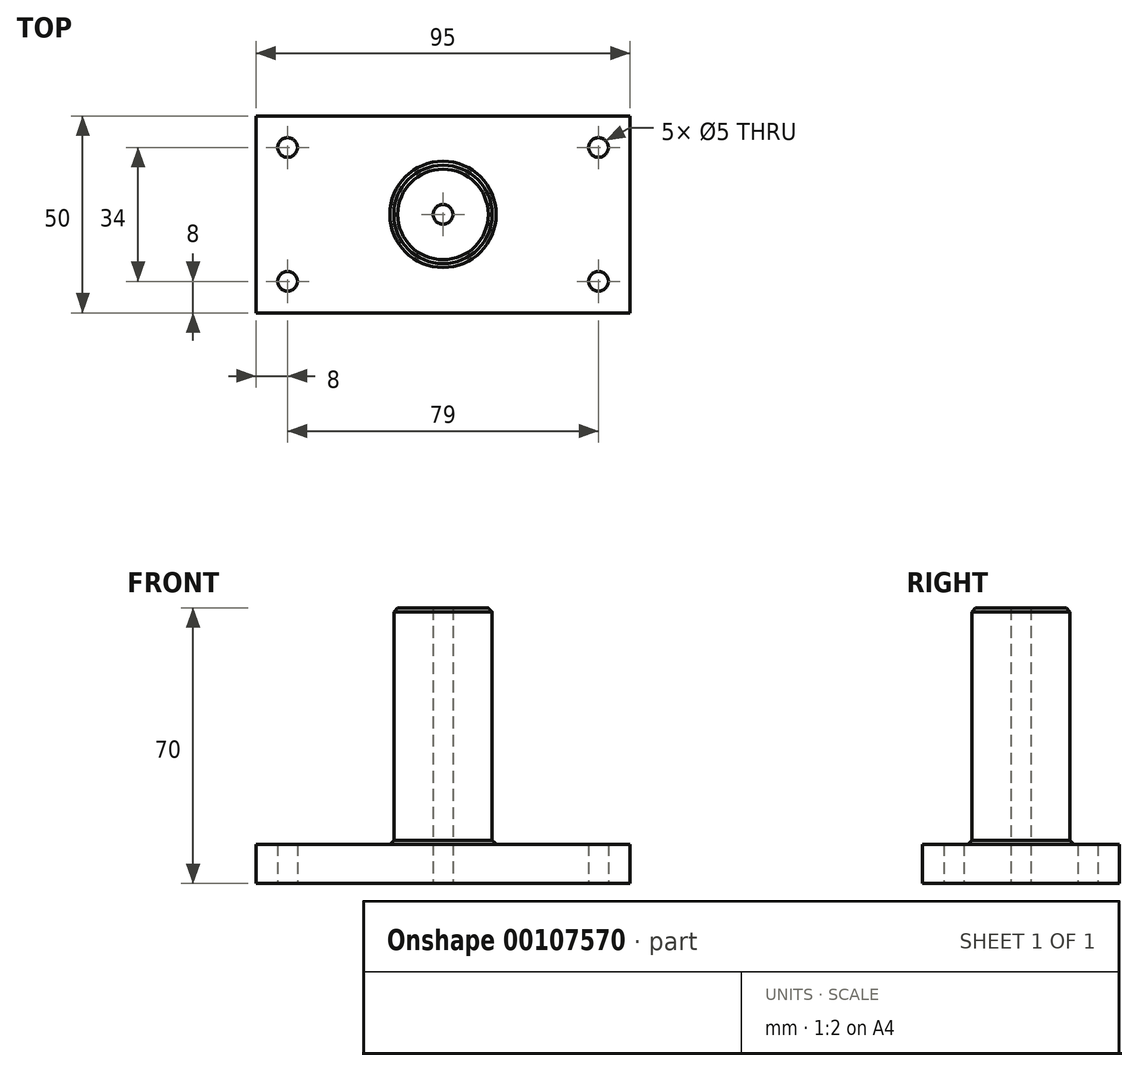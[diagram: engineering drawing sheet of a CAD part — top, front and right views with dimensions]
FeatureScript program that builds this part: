
annotation { "Feature Type Name" : "Feature", "Feature Type Description" : "" }
export const myFeature = defineFeature(function(context is Context, id is Id, definition is map)
    precondition{}
    {
        {
            var Q0;
            Q0=qCreatedBy(makeId("Top.planeOp"),FACE);
            var sketch = newSketch(context, id + "F0", { "sketchPlane" : qUnion([Q0])});
            skLineSegment(sketch, "E0.bottom", {"start": v(-47.5, 25) * mm, "end": v(47.5, 25) * mm});
            skLineSegment(sketch, "E0.top", {"start": v(-47.5, -25) * mm, "end": v(47.5, -25) * mm});
            skLineSegment(sketch, "E0.left", {"start": v(-47.5, 25) * mm, "end": v(-47.5, -25) * mm});
            skLineSegment(sketch, "E0.right", {"start": v(47.5, 25) * mm, "end": v(47.5, -25) * mm});
            skPoint(sketch, "E0.middle", {"position": v(0, 0) * mm});
            skCircle(sketch, "E1", {"center": v(39.5, -17) * mm, "radius": 2.5 * mm});
            skCircle(sketch, "E2", {"center": v(39.5, 17) * mm, "radius": 2.5 * mm});
            skCircle(sketch, "E3", {"center": v(-39.5, 17) * mm, "radius": 2.5 * mm});
            skCircle(sketch, "E4", {"center": v(-39.5, -17) * mm, "radius": 2.5 * mm});
            skSolve(sketch);
        }
        {
            var Q0;
            Q0=makeQuery(id+"F0.imprint","IMPRINT",FACE,{"disambiguationData":[TD([[makeQuery(id+"F0.imprint","IMPRINT",EDGE,{"derivedFrom":sQuery(id+"F0.wireOp",EDGE,"E0.bottom")}),-1.0]])]});
            extrude(context, id + "F1", {"entities" : qUnion([Q0]), "depth" : 10 * mm});
        }
        {
            var Q0;
            Q0=qCreatedBy(makeId("Top.planeOp"),FACE);
            var sketch = newSketch(context, id + "F2", { "sketchPlane" : qUnion([Q0])});
            skCircle(sketch, "E5", {"center": v(0, 0) * mm, "radius": 12.5 * mm});
            skCircle(sketch, "E6", {"center": v(0, 0) * mm, "radius": 2.5 * mm});
            skSolve(sketch);
        }
        {
            var Q0;
            Q0=makeQuery(id+"F2.imprint","IMPRINT",FACE,{"disambiguationData":[TD([[makeQuery(id+"F2.imprint","IMPRINT",EDGE,{"derivedFrom":sQuery(id+"F2.wireOp",EDGE,"E5")}),1.0]])]});
            extrude(context, id + "F3", {"entities" : qUnion([Q0]), "operationType" : NewBodyOperationType.ADD, "depth" : 70 * mm});
        }
        {
            var Q0;
            Q0=makeQuery(id+"F3.boolean.opBoolean","SPLIT",FACE,{"disambiguationData":[TD([makeQuery(id+"F3.opExtrude","SWEPT_FACE",FACE,{"disambiguationData":[OSD([sQuery(id+"F2.wireOp",EDGE,"E6")])]})])],"derivedFrom":makeQuery(id+"F1.opExtrude","CAP_FACE",FACE,{"disambiguationData":[OSD([sQuery(id+"F0.wireOp",EDGE,"E0.bottom"),sQuery(id+"F0.wireOp",EDGE,"E0.top"),sQuery(id+"F0.wireOp",EDGE,"E0.left"),sQuery(id+"F0.wireOp",EDGE,"E0.right"),sQuery(id+"F0.wireOp",EDGE,"E1"),sQuery(id+"F0.wireOp",EDGE,"E2"),sQuery(id+"F0.wireOp",EDGE,"E3"),sQuery(id+"F0.wireOp",EDGE,"E4")])],"isStart":false})});
            extrude(context, id + "F4", {"entities" : qUnion([Q0]), "operationType" : NewBodyOperationType.REMOVE, "oppositeDirection" : true, "depth" : 100 * mm});
        }
        {
            var Q0;
            Q0=makeQuery(id+"F3.opExtrude","CAP_EDGE",EDGE,{"disambiguationData":[OSD([sQuery(id+"F2.wireOp",EDGE,"E5")])],"isStart":false});
            var Q1;
            Q1=makeQuery(id+"F3.boolean.opBoolean","INTERSECT",EDGE,{"derivedFrom":[makeQuery(id+"F1.opExtrude","CAP_FACE",FACE,{"disambiguationData":[OSD([sQuery(id+"F0.wireOp",EDGE,"E0.bottom"),sQuery(id+"F0.wireOp",EDGE,"E0.top"),sQuery(id+"F0.wireOp",EDGE,"E0.left"),sQuery(id+"F0.wireOp",EDGE,"E0.right"),sQuery(id+"F0.wireOp",EDGE,"E1"),sQuery(id+"F0.wireOp",EDGE,"E2"),sQuery(id+"F0.wireOp",EDGE,"E3"),sQuery(id+"F0.wireOp",EDGE,"E4")])],"isStart":false}),makeQuery(id+"F3.opExtrude","SWEPT_FACE",FACE,{"disambiguationData":[OSD([sQuery(id+"F2.wireOp",EDGE,"E5")])]})]});
            chamfer(context, id + "F5", {"entities" : qUnion([Q0, Q1]), "width" : 1 * mm, "tangentPropagation" : true});
        }
    });
